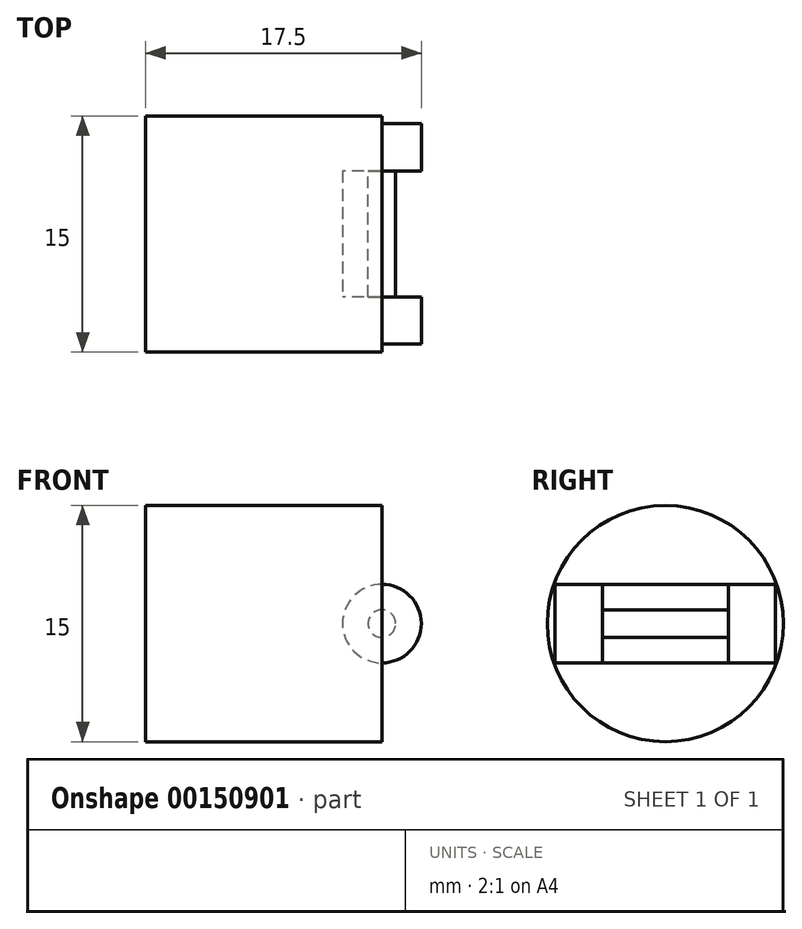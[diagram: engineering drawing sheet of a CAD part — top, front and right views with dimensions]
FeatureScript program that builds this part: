
annotation { "Feature Type Name" : "Feature", "Feature Type Description" : "" }
export const myFeature = defineFeature(function(context is Context, id is Id, definition is map)
    precondition{}
    {
        {
            var Q0;
            Q0=qCreatedBy(makeId("Right.planeOp"),FACE);
            var sketch = newSketch(context, id + "F0", { "sketchPlane" : qUnion([Q0])});
            skCircle(sketch, "E0", {"center": v(0, 0) * mm, "radius": 7.5 * mm});
            skSolve(sketch);
        }
        {
            var Q0;
            Q0=qSketchRegion(id+"F0",true);
            extrude(context, id + "F1", {"entities" : qUnion([Q0]), "endBound" : BoundingType.SYMMETRIC, "depth" : 15 * mm});
        }
        {
            var Q0;
            Q0=qCreatedBy(makeId("Front.planeOp"),FACE);
            var sketch = newSketch(context, id + "F2", { "sketchPlane" : qUnion([Q0])});
            skCircle(sketch, "E1", {"center": v(7.5, 0) * mm, "radius": 2.5 * mm});
            skSolve(sketch);
        }
        {
            var Q0;
            Q0=qSketchRegion(id+"F2",true);
            extrude(context, id + "F3", {"entities" : qUnion([Q0]), "operationType" : NewBodyOperationType.ADD, "endBound" : BoundingType.SYMMETRIC, "depth" : 14 * mm});
        }
        {
            var Q0;
            Q0=qCreatedBy(makeId("Front.planeOp"),FACE);
            var sketch = newSketch(context, id + "F4", { "sketchPlane" : qUnion([Q0])});
            skCircle(sketch, "E2", {"center": v(7.5, 0) * mm, "radius": 2.5 * mm});
            skSolve(sketch);
        }
        {
            var Q0;
            Q0=qSketchRegion(id+"F4",true);
            extrude(context, id + "F5", {"entities" : qUnion([Q0]), "operationType" : NewBodyOperationType.REMOVE, "endBound" : BoundingType.SYMMETRIC, "oppositeDirection" : true, "depth" : 8 * mm});
        }
        {
            var Q0;
            Q0=qCreatedBy(makeId("Front.planeOp"),FACE);
            var sketch = newSketch(context, id + "F6", { "sketchPlane" : qUnion([Q0])});
            skCircle(sketch, "E3", {"center": v(7.5, 0) * mm, "radius": 0.88 * mm});
            skSolve(sketch);
        }
        {
            var Q0;
            Q0=qSketchRegion(id+"F6",true);
            extrude(context, id + "F7", {"entities" : qUnion([Q0]), "operationType" : NewBodyOperationType.ADD, "endBound" : BoundingType.SYMMETRIC, "depth" : 8 * mm});
        }
    });
